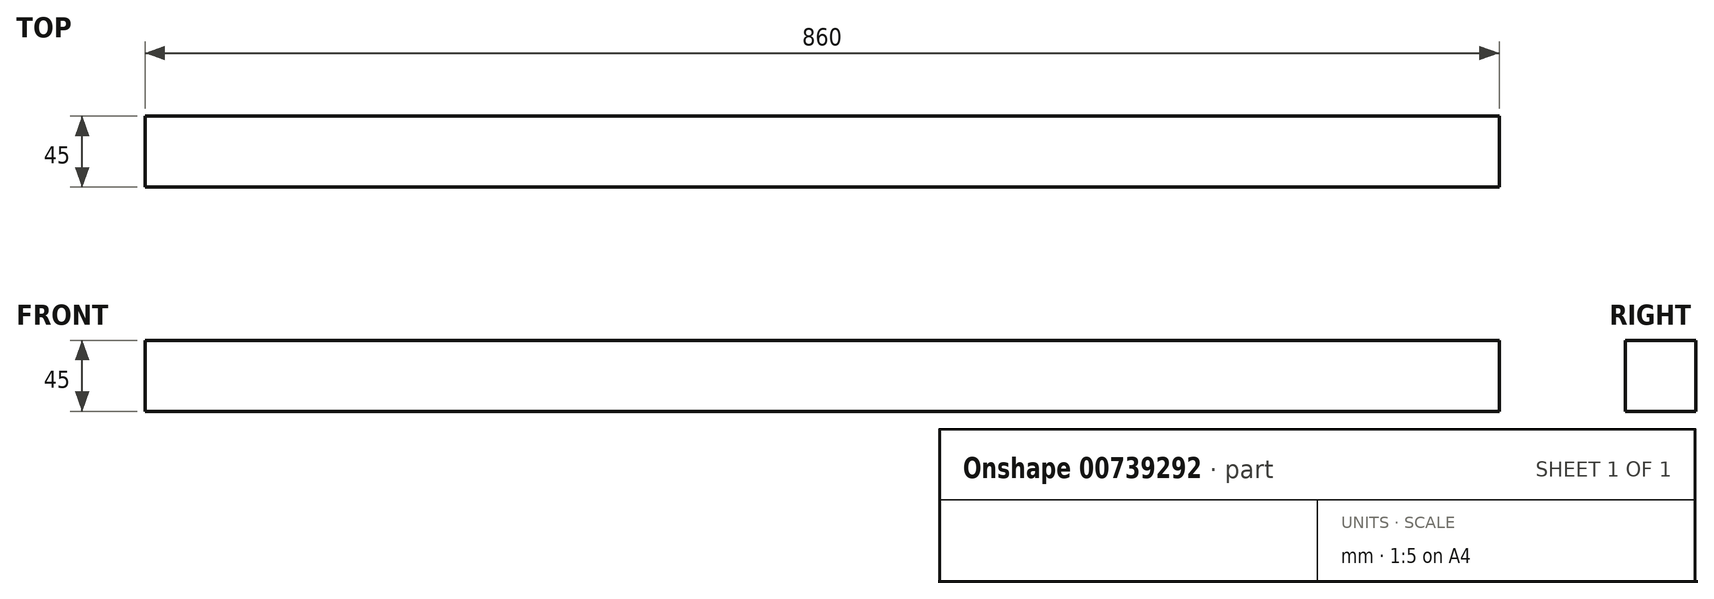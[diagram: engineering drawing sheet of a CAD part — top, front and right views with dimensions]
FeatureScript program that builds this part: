
annotation { "Feature Type Name" : "Feature", "Feature Type Description" : "" }
export const myFeature = defineFeature(function(context is Context, id is Id, definition is map)
    precondition{}
    {
        {
            var Q0;
            Q0=qCreatedBy(makeId("Right.planeOp"),FACE);
            var sketch = newSketch(context, id + "F0", { "sketchPlane" : qUnion([Q0])});
            skLineSegment(sketch, "E0", {"start": v(0, 45) * mm, "end": v(0, 0) * mm});
            skLineSegment(sketch, "E1", {"start": v(0, 0) * mm, "end": v(45, 0) * mm});
            skLineSegment(sketch, "E2", {"start": v(45, 0) * mm, "end": v(45, 45) * mm});
            skLineSegment(sketch, "E3", {"start": v(45, 45) * mm, "end": v(0, 45) * mm});
            skSolve(sketch);
        }
        {
            var Q0;
            Q0=makeQuery(id+"F0.imprint","IMPRINT",FACE,{"disambiguationData":[TD([[makeQuery(id+"F0.imprint","IMPRINT",EDGE,{"derivedFrom":sQuery(id+"F0.wireOp",EDGE,"E0")}),1.0]])]});
            extrude(context, id + "F1", {"entities" : qUnion([Q0]), "depth" : 860 * mm, "offsetDistance" : 25 * mm});
        }
    });
